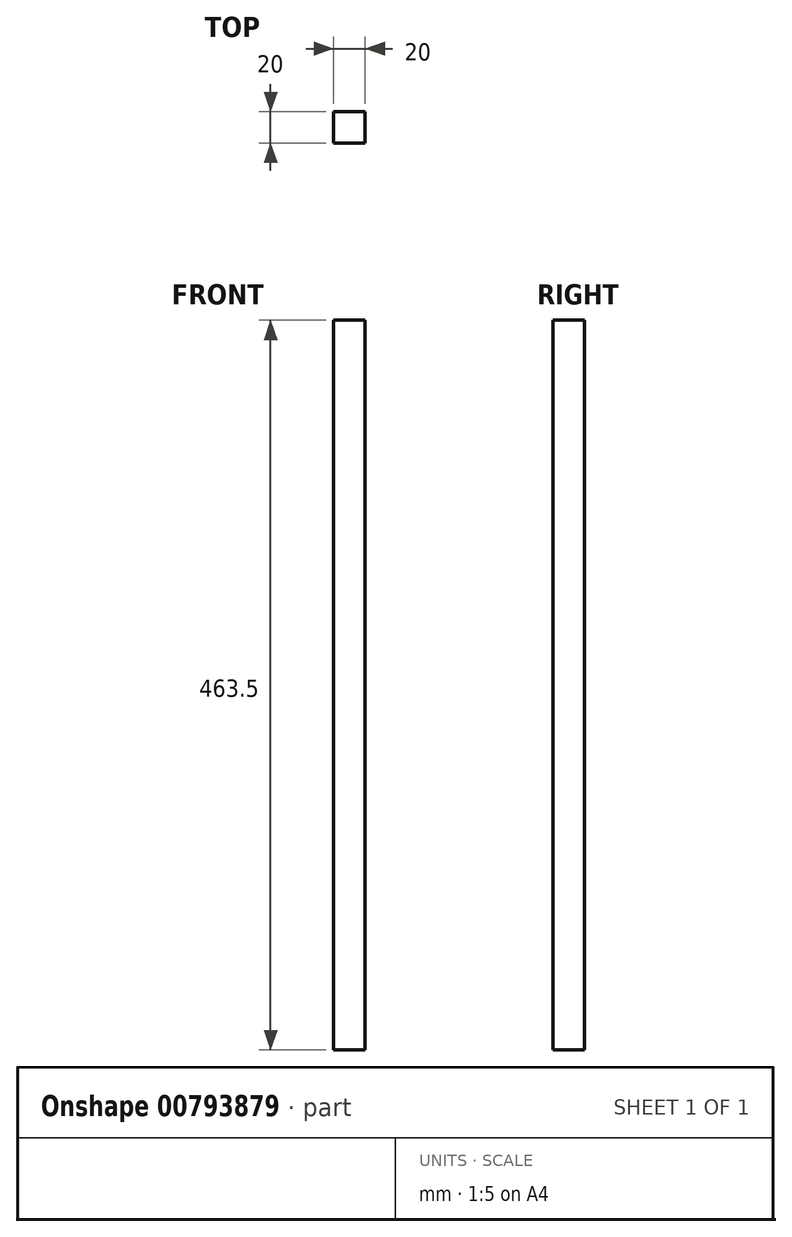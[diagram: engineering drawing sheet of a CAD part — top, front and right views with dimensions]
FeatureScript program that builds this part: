
annotation { "Feature Type Name" : "Feature", "Feature Type Description" : "" }
export const myFeature = defineFeature(function(context is Context, id is Id, definition is map)
    precondition{}
    {
        {
            var Q0;
            Q0=qCreatedBy(makeId("Top.planeOp"),FACE);
            var sketch = newSketch(context, id + "F0", { "sketchPlane" : qUnion([Q0])});
            skLineSegment(sketch, "E0.bottom", {"start": v(-10, 10) * mm, "end": v(10, 10) * mm});
            skLineSegment(sketch, "E0.top", {"start": v(-10, -10) * mm, "end": v(10, -10) * mm});
            skLineSegment(sketch, "E0.left", {"start": v(-10, 10) * mm, "end": v(-10, -10) * mm});
            skLineSegment(sketch, "E0.right", {"start": v(10, 10) * mm, "end": v(10, -10) * mm});
            skSolve(sketch);
        }
        {
            var Q0;
            Q0=qSketchRegion(id+"F0",true);
            extrude(context, id + "F1", {"entities" : qUnion([Q0]), "depth" : 463.5 * mm, "offsetDistance" : 25 * mm});
        }
    });
